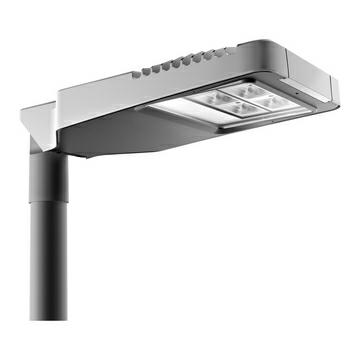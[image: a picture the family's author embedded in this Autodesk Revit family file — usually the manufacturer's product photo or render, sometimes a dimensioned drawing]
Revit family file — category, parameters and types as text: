
# Revit family: Lighting-StreetLighting-GEWISS-ROAD[5]MINI-LED_OPTIC_WIDE-W_CLII
name_source: partatom
category: Apparecchi per illuminazione
units: mm (PartAtom-declared; Revit-internal decimal feet)

## family parameters
Basato su piano di lavoro = No
Condiviso = No
Punto di calcolo locali = No
Quota connettore circolare = Usa diametro
Sempre verticale = Sì
Sorgente d'illuminazione = No
Taglio con vuoti quando caricato = No
Tipo di parte = Normale

## types (6) — shared parameters
Applicazione = External
Body = Die-cast aluminium -
Carico apparente = 54 VA
Catalogue = LIGHTING
Catalogue Range = ROAD [5]
Classification: = -
Color Rendering Index = CRI-70
Colore = Graphite grey
Colour : = Powder coating
Colour temperature = 4000K
Colour temperature: = 4000 K (CRI>70)
Commenti sul wattaggio = 54W
Context = Street and parking lighting
Control System = Bi-power with self-learning
DIN 18032-3 certification = -
Device with reduced surface temperature = -
Driver = Included
Driver Box = Built-in
Electrocod = 244C
Eletrical and lighting features = -
External screw = Stainless steel
Fixing = Pole Head - Outreach
Gasket = Anti-aging silicone
General information = -
Glow Wire Test : = -
IDF = 6b7a7611-5164-418c-9daf-cb576d1309ef
IDT = 7b37660f6c27427dab2b33d7b45cf4bf
IP degree = IP66
Immagine tipo = GWR5276M.jpg
Installationa and maintenance = -
Insulation class = II
LED Life time (L80B10) = 100000H
LED Maintenance = Not available
Lamp- = LED
Lifetime = L90B10 (Tq+25°C) = 100.000 h
Locking Hook = Integrated front handle
Luminaire = LED Road Equipment
Materials = -
Maximum surface exposed to the wind = 0,149999999999999M2
Maximum surface exposed to the wind : = 0.15 m²
Minimum distance from the illuminated object = 1M
Mouting and installation = Pole Head - Outreach
Optic = WIDE
Optic : = Metallized polycarbonate reflector
Optic Maintenance = Not available
Optic and illuminating features = -
Overvoltage protection = DM 10KV / CM 10KV
Overvoltage resistance = 10 KV (Common mode)
Photobiological Risk Class = RG0
Produttore = GEWISS S.p.A.
Rated frequency (Hz) = 50 / 60
SEO = Street lighting
Shield type = 4mm thick flat tempered glass
Shock resistance = IK08
Standard Deviation Colour Matching = SDCM = 5
Standard- = EN 60598-2-3, EN 60598-1 IEC/TR 62778
Standards and approvals = -
Stocking temperature = -
Supply voltage = 220 - 240 V
Technical sheet = https://www.gewiss.com
Tilt adjustable = -20° ÷ +10° side bracket - -10° ÷ +20° pole head
Tilt- = -20° ÷ +10° side bracket - -10° ÷ +20° pole head
Tipo alimentatore = Constant Current Driver Led
Tipologia = Bi power
Type of light source = LED - Not replaceable
URL = https://www.gewiss.com
Unified Glare Rating = G*4 - ULOR = 0
Unique digital code (Datamatrix) = Currently not present
Version file RFA = 20.11
Warranty = 5 years
Wiring = Isolating switch

## per-type parameters (varying)
| type | Efficiency (lm/W) | IPEA | LED current. | Lumen output (lm) | Modello | Number of modules | Operating temperature : | Operating temperature: | System power | System power : | Voltage- | Weight (kg): |
| GWR5271BW - ROAD5 MINI WIDE 1M 4000K 0,7A CL2 BIR.W | 112 | ROAD = A4 + // LARGE AREAS = A5 + // CYCLOPEDONALS = A3 + // GREEN AREAS = A3 + // HISTORICAL CENTER = A6 + | 0,35A | 5600 | GWR5271BW | 1 (1x3 LED) | -25 +40 °C | -25 +40 °C | 50W | 50 W @ 0.7A | 220/240 V - 50/60 Hz | 6,4 |
| GWR5232BW - ROAD5 MINI WIDE 2M 4000K 0,35A CL2 BI.W | 120 | ROAD = A5 + // LARGE AREAS = A6 + // CYCLOPEDONALS = A5 + // GREEN AREAS = A5 + // HISTORICAL CENTER = A6 + | 0,35A | 6000 | GWR5232BW | 2 (2x3 LED) | -25 +40 °C | -25 +40 °C | 50W | 50 W @ 0.35A | 220/240 V - 50/60 Hz | 6,59999999999999 |
| GWR5231BW - ROAD5 MINI WIDE 1M 4000K 0,35A CL2 BI.W | 115 | ROAD = A4 + // LARGE AREAS = A5 + // CYCLOPEDONALS = A4 + // GREEN AREAS = A4 + // HISTORICAL CENTER = A6 + | 0,35A | 3100 | GWR5231BW | 1 (1x3 LED) | -25 +40 °C | -25 +40 °C | 27W | 27 W @ 0.35A | 220/240 V - 50/60 Hz | 6,4 |
| GWR5252BW - ROAD5 MINI WIDE 2M 4000K 0,50A CL2 BI.W | 111 | ROAD = A3 + // LARGE AREAS = A4 + // CYCLOPEDONALS = A ++ // GREEN AREAS = A ++ // HISTORICAL CENTER = A6 + | 0,5A | 8100 | GWR5252BW | 2 (2x3 LED) | -25 +30 °C | -25 +30 °C | 73W | 73 W @ 0.5A | 220 / 240 V - 50 / 60 Hz | 6,59999999999999 |
| GWR5272BW - ROAD5 MINI WIDE 2M 4000K 0,7A CL2 BIR.W | 108 | ROAD = A ++ // LARGE AREAS = A4 + // CYCLOPEDONALS = A + // GREEN AREAS = A + // HISTORICAL CENTER = A5 + | 0,7A | 10800 | GWR5272BW | 2 (2x3 LED) | -25 +30 °C | -25 +30 °C | 100W | 100 W @ 0.7A | 220/240 V - 50/60 Hz | 6,59999999999999 |
| GWR5251BW - ROAD5 MINI WIDE 1M 4000K 0,50A CL2 BI.W | 114 | ROAD = A4 + // LARGE AREAS = A5 + // CYCLOPEDONALS = A4 + // GREEN AREAS = A4 + // HISTORICAL CENTER = A6 + | 0,5A | 4200 | GWR5251BW | 1 (1x3 LED) | -25 +40 °C | -25 +40 °C | 37W | 37 W @ 0.5A | 220 / 240 V - 50 / 60 Hz | 6,4 |

note: column(s) folded — value = type name in every type: Descrizione

## geometry (parser evidence)
native form markers: Blend x2
no freeform markers — native parametric forms only
